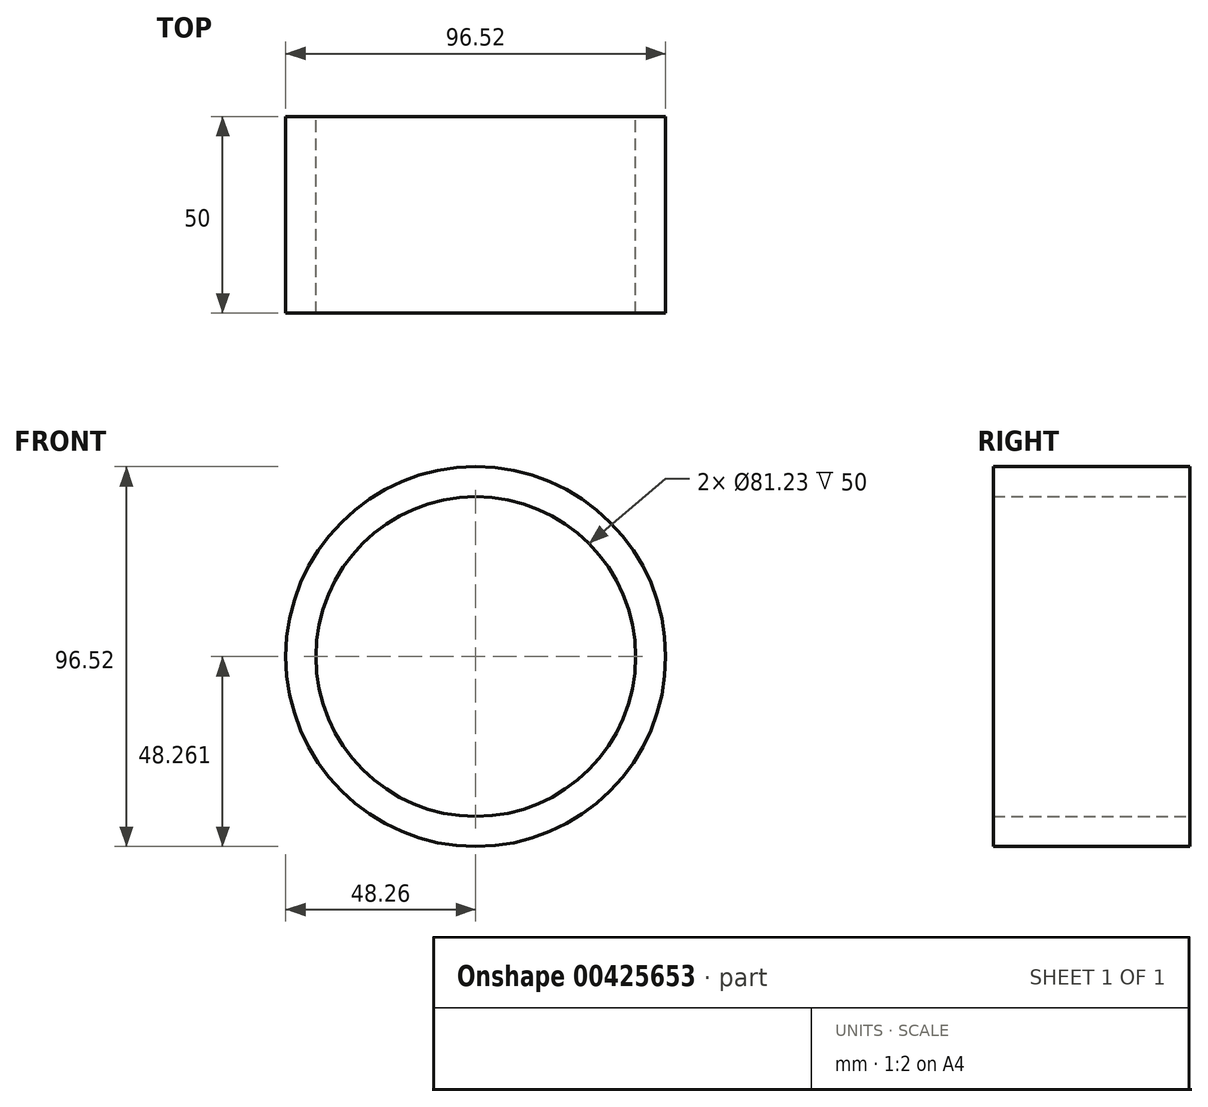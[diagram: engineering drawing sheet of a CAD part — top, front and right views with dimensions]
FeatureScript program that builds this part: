
annotation { "Feature Type Name" : "Feature", "Feature Type Description" : "" }
export const myFeature = defineFeature(function(context is Context, id is Id, definition is map)
    precondition{}
    {
        {
            var Q0;
            Q0=qCreatedBy(makeId("Top.planeOp"),FACE);
            var sketch = newSketch(context, id + "F0", { "sketchPlane" : qUnion([Q0])});
            skCircle(sketch, "E0", {"center": v(0, 0) * mm, "radius": 220 * mm});
            skSolve(sketch);
        }
        {
            var Q0;
            Q0=qCreatedBy(makeId("Front.planeOp"),FACE);
            var sketch = newSketch(context, id + "F1", { "sketchPlane" : qUnion([Q0])});
            skCircle(sketch, "E1", {"center": v(0, 61.24) * mm, "radius": 48.26 * mm});
            skCircle(sketch, "E2", {"center": v(0, 61.24) * mm, "radius": 40.62 * mm});
            skCircle(sketch, "E3", {"center": v(0, 61.24) * mm, "radius": 17.51 * mm});
            skSolve(sketch);
        }
        {
            var Q0;
            Q0=makeQuery(id+"F1.imprint","IMPRINT",FACE,{"disambiguationData":[TD([[makeQuery(id+"F1.imprint","IMPRINT",EDGE,{"derivedFrom":sQuery(id+"F1.wireOp",EDGE,"E1")}),1.0]])]});
            extrude(context, id + "F2", {"entities" : qUnion([Q0]), "depth" : 50 * mm});
        }
        {
            var Q0;
            Q0=makeQuery(id+"F2.opExtrude","SWEPT_BODY",BODY,{"disambiguationData":[OSD([sQuery(id+"F1.wireOp",EDGE,"E1"),sQuery(id+"F1.wireOp",EDGE,"E2")])]});
            transform(context, id + "F3", {"entities" : qUnion([Q0]), "transformType" : TransformType.TRANSLATION_3D, "dx" : 0 * mm, "dy" : 0 * mm, "dz" : 0 * mm, "makeCopy" : true});
        }
    });
